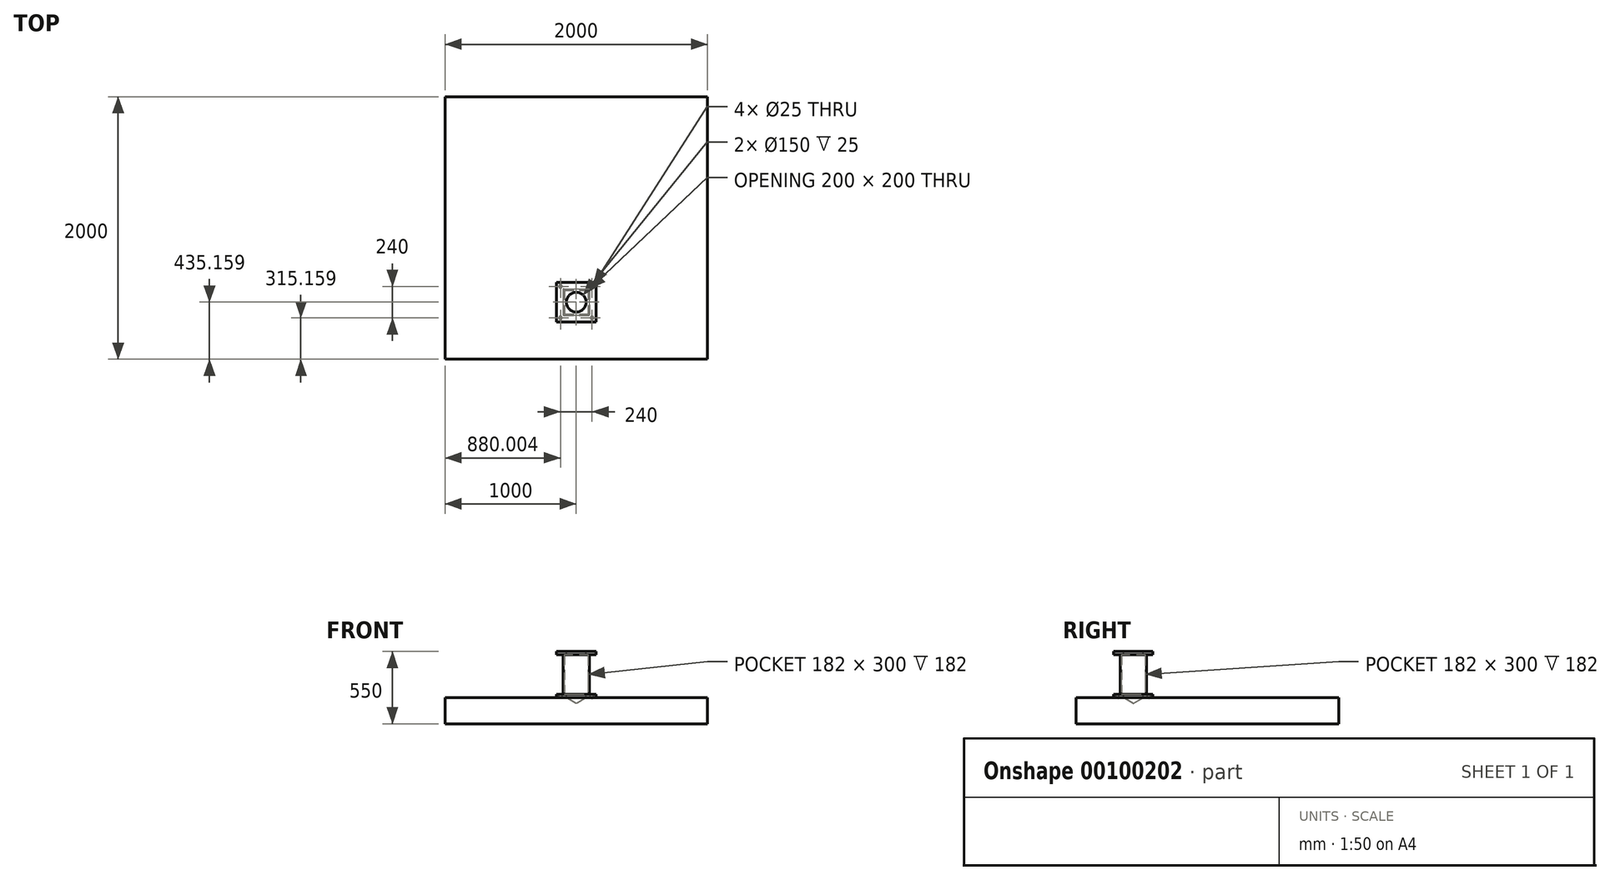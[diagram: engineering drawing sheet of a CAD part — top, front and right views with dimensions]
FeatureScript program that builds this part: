
annotation { "Feature Type Name" : "Feature", "Feature Type Description" : "" }
export const myFeature = defineFeature(function(context is Context, id is Id, definition is map)
    precondition{}
    {
        {
            var Q0;
            Q0=qCreatedBy(makeId("Top.planeOp"),FACE);
            var sketch = newSketch(context, id + "F0", { "sketchPlane" : qUnion([Q0])});
            skLineSegment(sketch, "E0.bottom", {"start": v(-1003.94, 1344.81) * mm, "end": v(996.06, 1344.81) * mm});
            skLineSegment(sketch, "E0.top", {"start": v(-1003.94, -655.19) * mm, "end": v(996.06, -655.19) * mm});
            skLineSegment(sketch, "E0.left", {"start": v(-1003.94, 1344.81) * mm, "end": v(-1003.94, -655.19) * mm});
            skLineSegment(sketch, "E0.right", {"start": v(996.06, 1344.81) * mm, "end": v(996.06, -655.19) * mm});
            skSolve(sketch);
        }
        {
            var Q0;
            Q0=makeQuery(id+"F0.imprint","IMPRINT",FACE,{"disambiguationData":[TD([[makeQuery(id+"F0.imprint","IMPRINT",EDGE,{"derivedFrom":sQuery(id+"F0.wireOp",EDGE,"E0.bottom")}),-1.0]])]});
            extrude(context, id + "F1", {"entities" : qUnion([Q0]), "depth" : 200 * mm});
        }
        {
            var Q0;
            Q0=makeQuery(id+"F1.opExtrude","CAP_FACE",FACE,{"disambiguationData":[OSD([sQuery(id+"F0.wireOp",EDGE,"E0.bottom"),sQuery(id+"F0.wireOp",EDGE,"E0.top"),sQuery(id+"F0.wireOp",EDGE,"E0.left"),sQuery(id+"F0.wireOp",EDGE,"E0.right")])],"isStart":false});
            var sketch = newSketch(context, id + "F2", { "sketchPlane" : qUnion([Q0])});
            skLineSegment(sketch, "E1.bottom", {"start": v(-153.94, -70.03) * mm, "end": v(146.06, -70.03) * mm});
            skLineSegment(sketch, "E1.top", {"start": v(-153.94, -370.03) * mm, "end": v(146.06, -370.03) * mm});
            skLineSegment(sketch, "E1.left", {"start": v(-153.94, -70.03) * mm, "end": v(-153.94, -370.03) * mm});
            skLineSegment(sketch, "E1.right", {"start": v(146.06, -70.03) * mm, "end": v(146.06, -370.03) * mm});
            skSolve(sketch);
        }
        {
            var Q0;
            Q0 = qSketchRegion(id + "F2", true);
            extrude(context, id + "F3", {"entities" : qUnion([Q0]), "operationType" : NewBodyOperationType.ADD, "depth" : 25 * mm});
        }
        {
            var Q0;
            Q0=makeQuery(id+"F3.opExtrude","CAP_FACE",FACE,{"disambiguationData":[OSD([sQuery(id+"F2.wireOp",EDGE,"E1.bottom"),sQuery(id+"F2.wireOp",EDGE,"E1.top"),sQuery(id+"F2.wireOp",EDGE,"E1.left"),sQuery(id+"F2.wireOp",EDGE,"E1.right")])],"isStart":false});
            var sketch = newSketch(context, id + "F4", { "sketchPlane" : qUnion([Q0])});
            skLineSegment(sketch, "E2.bottom", {"start": v(-123.94, -100.03) * mm, "end": v(116.06, -100.03) * mm, "construction": true});
            skLineSegment(sketch, "E2.top", {"start": v(-123.94, -340.03) * mm, "end": v(116.06, -340.03) * mm, "construction": true});
            skLineSegment(sketch, "E2.left", {"start": v(-123.94, -100.03) * mm, "end": v(-123.94, -340.03) * mm, "construction": true});
            skLineSegment(sketch, "E2.right", {"start": v(116.06, -100.03) * mm, "end": v(116.06, -340.03) * mm, "construction": true});
            skCircle(sketch, "E3", {"center": v(-123.94, -100.03) * mm, "radius": 11 * mm});
            skCircle(sketch, "E4", {"center": v(116.06, -100.03) * mm, "radius": 11 * mm});
            skCircle(sketch, "E5", {"center": v(-123.94, -340.03) * mm, "radius": 11 * mm});
            skCircle(sketch, "E6", {"center": v(116.06, -340.03) * mm, "radius": 11 * mm});
            skCircle(sketch, "E7", {"center": v(-3.94, -220.03) * mm, "radius": 75 * mm});
            skSolve(sketch);
        }
        {
            var Q0;
            Q0=sQuery(id+"F4.wireOp",VERTEX,"E2.left.start");
            var Q1;
            Q1=sQuery(id+"F4.wireOp",VERTEX,"E2.left.end");
            var Q2;
            Q2=sQuery(id+"F4.wireOp",VERTEX,"E2.top.end");
            var Q3;
            Q3=sQuery(id+"F4.wireOp",VERTEX,"E2.right.start");
            var Q4;
            Q4=makeQuery(id+"F1.opExtrude","SWEPT_BODY",BODY,{"disambiguationData":[OSD([sQuery(id+"F0.wireOp",EDGE,"E0.bottom"),sQuery(id+"F0.wireOp",EDGE,"E0.top"),sQuery(id+"F0.wireOp",EDGE,"E0.left"),sQuery(id+"F0.wireOp",EDGE,"E0.right")])]});
            hole(context, id + "F5", {"style" : HoleStyle.SIMPLE, "endStyle" : HoleEndStyle.BLIND, "holeDiameter" : 25 * mm, "holeDepth" : 25 * mm, "locations" : qUnion([Q0, Q1, Q2, Q3]), "scope" : qUnion([Q4])});
        }
        {
            var Q0;
            Q0=sQuery(id+"F4.wireOp",VERTEX,"E7.center");
            var Q1;
            Q1=makeQuery(id+"F1.opExtrude","SWEPT_BODY",BODY,{"disambiguationData":[OSD([sQuery(id+"F0.wireOp",EDGE,"E0.bottom"),sQuery(id+"F0.wireOp",EDGE,"E0.top"),sQuery(id+"F0.wireOp",EDGE,"E0.left"),sQuery(id+"F0.wireOp",EDGE,"E0.right")])]});
            hole(context, id + "F6", {"style" : HoleStyle.SIMPLE, "endStyle" : HoleEndStyle.BLIND, "holeDiameter" : 150 * mm, "holeDepth" : 25 * mm, "locations" : qUnion([Q0]), "scope" : qUnion([Q1])});
        }
        {
            var Q0;
            Q0=makeQuery(id+"F3.opExtrude","CAP_FACE",FACE,{"disambiguationData":[OSD([sQuery(id+"F2.wireOp",EDGE,"E1.bottom"),sQuery(id+"F2.wireOp",EDGE,"E1.top"),sQuery(id+"F2.wireOp",EDGE,"E1.left"),sQuery(id+"F2.wireOp",EDGE,"E1.right")])],"isStart":false});
            var sketch = newSketch(context, id + "F7", { "sketchPlane" : qUnion([Q0])});
            skLineSegment(sketch, "E8.bottom", {"start": v(-98.94, -120.03) * mm, "end": v(91.06, -120.03) * mm});
            skLineSegment(sketch, "E8.top", {"start": v(-98.94, -320.03) * mm, "end": v(91.06, -320.03) * mm});
            skLineSegment(sketch, "E8.left", {"start": v(-103.94, -125.03) * mm, "end": v(-103.94, -315.03) * mm});
            skLineSegment(sketch, "E8.right", {"start": v(96.06, -125.03) * mm, "end": v(96.06, -315.03) * mm});
            skPoint(sketch, "E9.visualSharp", {"position": v(-103.94, -120.03) * mm});
            skArc(sketch, "E9.filletArc", {"start": v(-98.94, -120.03) * mm, "mid": v(-102.47, -121.5) * mm, "end": v(-103.94, -125.03) * mm});
            skPoint(sketch, "E10.visualSharp", {"position": v(96.06, -120.03) * mm});
            skArc(sketch, "E10.filletArc", {"start": v(96.06, -125.03) * mm, "mid": v(94.6, -121.5) * mm, "end": v(91.06, -120.03) * mm});
            skPoint(sketch, "E11.visualSharp", {"position": v(96.06, -320.03) * mm});
            skArc(sketch, "E11.filletArc", {"start": v(91.06, -320.03) * mm, "mid": v(94.6, -318.57) * mm, "end": v(96.06, -315.03) * mm});
            skPoint(sketch, "E12.visualSharp", {"position": v(-103.94, -320.03) * mm});
            skArc(sketch, "E12.filletArc", {"start": v(-103.94, -315.03) * mm, "mid": v(-102.47, -318.57) * mm, "end": v(-98.94, -320.03) * mm});
            skLineSegment(sketch, "E13.0", {"start": v(-94.94, -129.03) * mm, "end": v(-94.94, -311.03) * mm});
            skLineSegment(sketch, "E14.0", {"start": v(-94.94, -129.03) * mm, "end": v(87.06, -129.03) * mm});
            skLineSegment(sketch, "E15.0", {"start": v(87.06, -129.03) * mm, "end": v(87.06, -311.03) * mm});
            skLineSegment(sketch, "E16.0", {"start": v(-94.94, -311.03) * mm, "end": v(87.06, -311.03) * mm});
            skSolve(sketch);
        }
        {
            var Q0;
            Q0 = qSketchRegion(id + "F7", true);
            extrude(context, id + "F8", {"entities" : qUnion([Q0]), "operationType" : NewBodyOperationType.ADD, "depth" : 300 * mm});
        }
        {
            var Q0;
            Q0=makeQuery(id+"F8.opExtrude","CAP_FACE",FACE,{"disambiguationData":[OSD([sQuery(id+"F7.wireOp",EDGE,"E8.bottom"),sQuery(id+"F7.wireOp",EDGE,"E8.top"),sQuery(id+"F7.wireOp",EDGE,"E8.left"),sQuery(id+"F7.wireOp",EDGE,"E8.right"),sQuery(id+"F7.wireOp",EDGE,"E9.filletArc"),sQuery(id+"F7.wireOp",EDGE,"E10.filletArc"),sQuery(id+"F7.wireOp",EDGE,"E11.filletArc"),sQuery(id+"F7.wireOp",EDGE,"E12.filletArc"),sQuery(id+"F7.wireOp",EDGE,"E13.0"),sQuery(id+"F7.wireOp",EDGE,"E14.0"),sQuery(id+"F7.wireOp",EDGE,"E15.0"),sQuery(id+"F7.wireOp",EDGE,"E16.0")])],"isStart":false});
            var sketch = newSketch(context, id + "F9", { "sketchPlane" : qUnion([Q0])});
            skLineSegment(sketch, "E17.bottom", {"start": v(-153.94, -70.03) * mm, "end": v(146.06, -70.03) * mm});
            skLineSegment(sketch, "E17.top", {"start": v(-153.94, -370.03) * mm, "end": v(146.06, -370.03) * mm});
            skLineSegment(sketch, "E17.left", {"start": v(-153.94, -70.03) * mm, "end": v(-153.94, -370.03) * mm});
            skLineSegment(sketch, "E17.right", {"start": v(146.06, -70.03) * mm, "end": v(146.06, -370.03) * mm});
            skSolve(sketch);
        }
        {
            var Q0;
            Q0 = qSketchRegion(id + "F9", true);
            extrude(context, id + "F10", {"entities" : qUnion([Q0]), "operationType" : NewBodyOperationType.ADD, "depth" : 25 * mm});
        }
        {
            var Q0;
            Q0=makeQuery(id+"F10.opExtrude","CAP_FACE",FACE,{"disambiguationData":[OSD([sQuery(id+"F9.wireOp",EDGE,"E17.bottom"),sQuery(id+"F9.wireOp",EDGE,"E17.top"),sQuery(id+"F9.wireOp",EDGE,"E17.left"),sQuery(id+"F9.wireOp",EDGE,"E17.right")])],"isStart":false});
            var sketch = newSketch(context, id + "F11", { "sketchPlane" : qUnion([Q0])});
            skCircle(sketch, "E18", {"center": v(-3.94, -220.03) * mm, "radius": 60.07 * mm});
            skSolve(sketch);
        }
        {
            var Q0;
            Q0=sQuery(id+"F11.wireOp",VERTEX,"E18.center");
            var Q1;
            Q1=makeQuery(id+"F1.opExtrude","SWEPT_BODY",BODY,{"disambiguationData":[OSD([sQuery(id+"F0.wireOp",EDGE,"E0.bottom"),sQuery(id+"F0.wireOp",EDGE,"E0.top"),sQuery(id+"F0.wireOp",EDGE,"E0.left"),sQuery(id+"F0.wireOp",EDGE,"E0.right")])]});
            hole(context, id + "F12", {"style" : HoleStyle.SIMPLE, "endStyle" : HoleEndStyle.BLIND, "holeDiameter" : 150 * mm, "holeDepth" : 25 * mm, "locations" : qUnion([Q0]), "scope" : qUnion([Q1])});
        }
    });
